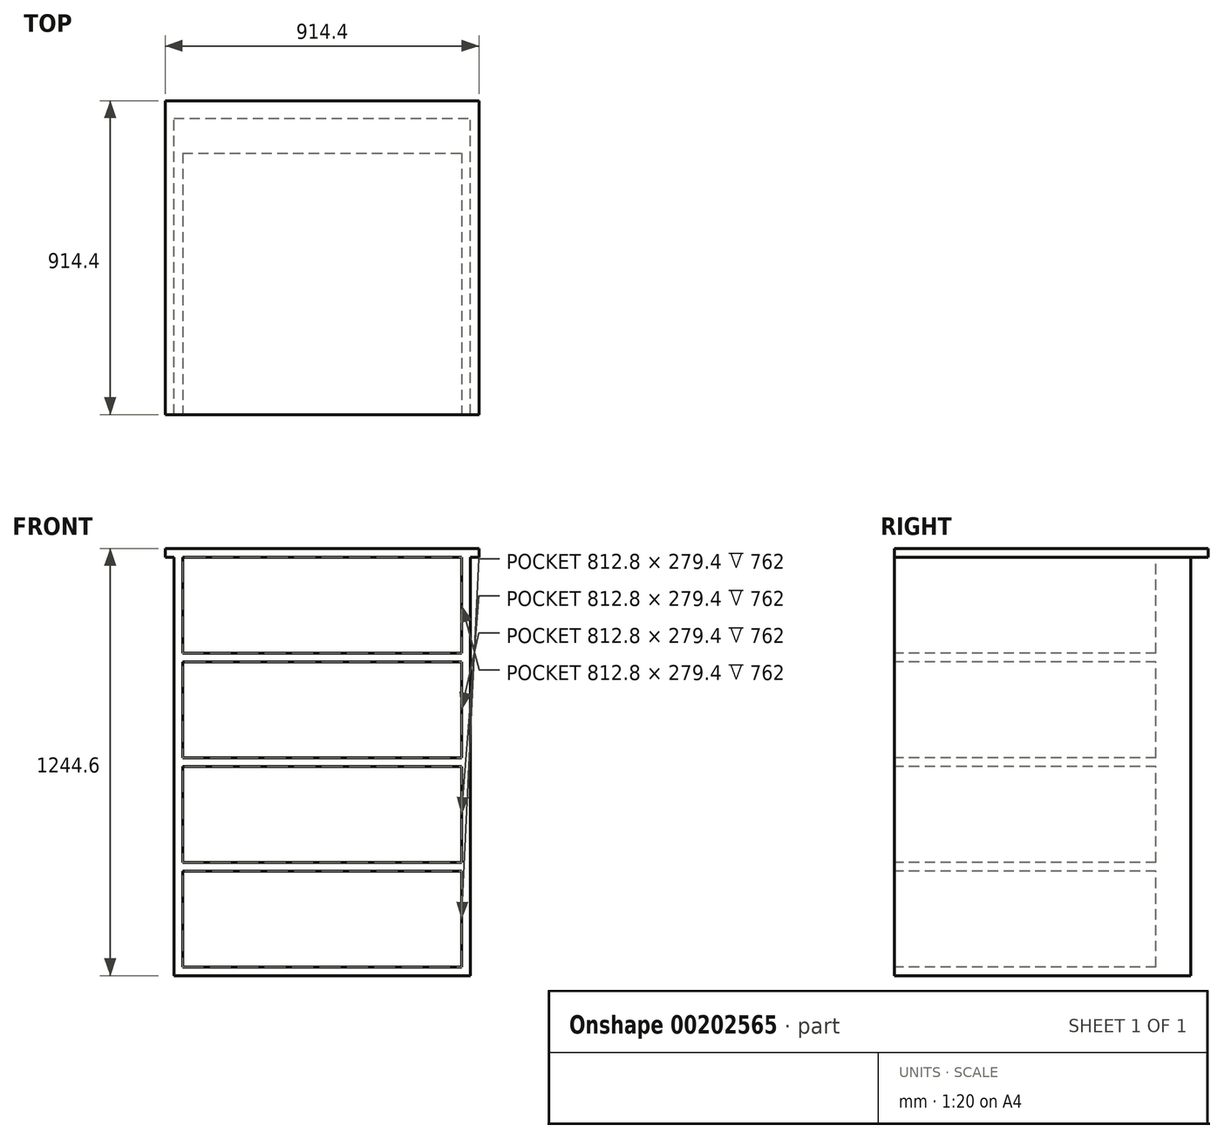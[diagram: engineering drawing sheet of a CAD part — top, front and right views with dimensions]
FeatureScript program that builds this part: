
annotation { "Feature Type Name" : "Feature", "Feature Type Description" : "" }
export const myFeature = defineFeature(function(context is Context, id is Id, definition is map)
    precondition{}
    {
        {
            var Q0;
            Q0=qCreatedBy(makeId("Top.planeOp"),FACE);
            var sketch = newSketch(context, id + "F0", { "sketchPlane" : qUnion([Q0])});
            skLineSegment(sketch, "E0.bottom", {"start": v(3.96, 0) * mm, "end": v(867.56, 0) * mm});
            skLineSegment(sketch, "E0.top", {"start": v(3.96, 863.6) * mm, "end": v(867.56, 863.6) * mm});
            skLineSegment(sketch, "E0.left", {"start": v(3.96, 0) * mm, "end": v(3.96, 863.6) * mm});
            skLineSegment(sketch, "E0.right", {"start": v(867.56, 0) * mm, "end": v(867.56, 863.6) * mm});
            skSolve(sketch);
        }
        {
            var Q0;
            Q0 = qSketchRegion(id + "F0", true);
            extrude(context, id + "F1", {"entities" : qUnion([Q0]), "depth" : 1219.2 * mm});
        }
        {
            var Q0;
            Q0=makeQuery(id+"F1.opExtrude","CAP_FACE",FACE,{"disambiguationData":[OSD([sQuery(id+"F0.wireOp",EDGE,"E0.bottom"),sQuery(id+"F0.wireOp",EDGE,"E0.top"),sQuery(id+"F0.wireOp",EDGE,"E0.left"),sQuery(id+"F0.wireOp",EDGE,"E0.right")])],"isStart":false});
            var sketch = newSketch(context, id + "F2", { "sketchPlane" : qUnion([Q0])});
            skLineSegment(sketch, "E1", {"start": v(867.56, 0) * mm, "end": v(892.96, 0) * mm});
            skLineSegment(sketch, "E2", {"start": v(892.96, 0) * mm, "end": v(892.96, 914.4) * mm});
            skLineSegment(sketch, "E3", {"start": v(892.96, 914.4) * mm, "end": v(-21.44, 914.4) * mm});
            skLineSegment(sketch, "E4", {"start": v(-21.44, 914.4) * mm, "end": v(-21.44, 0) * mm});
            skLineSegment(sketch, "E5", {"start": v(-21.44, 0) * mm, "end": v(3.96, 0) * mm});
            skLineSegment(sketch, "E6.bottom", {"start": v(867.56, 0) * mm, "end": v(3.96, 0) * mm});
            skLineSegment(sketch, "E6.top", {"start": v(867.56, 863.6) * mm, "end": v(3.96, 863.6) * mm});
            skLineSegment(sketch, "E6.left", {"start": v(867.56, 0) * mm, "end": v(867.56, 863.6) * mm});
            skLineSegment(sketch, "E6.right", {"start": v(3.96, 0) * mm, "end": v(3.96, 863.6) * mm});
            skSolve(sketch);
        }
        {
            var Q0;
            Q0 = qSketchRegion(id + "F2", true);
            extrude(context, id + "F3", {"entities" : qUnion([Q0]), "operationType" : NewBodyOperationType.ADD, "depth" : 25.4 * mm});
        }
        {
            var Q0;
            Q0=makeQuery(id+"F3.boolean.opBoolean","MERGE",FACE,{"derivedFrom":[makeQuery(id+"F1.opExtrude","SWEPT_FACE",FACE,{"disambiguationData":[OSD([sQuery(id+"F0.wireOp",EDGE,"E0.bottom")])]}),makeQuery(id+"F3.opExtrude","SWEPT_FACE",FACE,{"disambiguationData":[OSD([sQuery(id+"F2.wireOp",EDGE,"E1"),sQuery(id+"F2.wireOp",EDGE,"E5"),sQuery(id+"F2.wireOp",EDGE,"E6.bottom")])]})]});
            var sketch = newSketch(context, id + "F4", { "sketchPlane" : qUnion([Q0])});
            skLineSegment(sketch, "E7", {"start": v(3.96, 0) * mm, "end": v(3.96, 25.4) * mm});
            skLineSegment(sketch, "E8", {"start": v(3.96, 25.4) * mm, "end": v(29.36, 25.4) * mm});
            skLineSegment(sketch, "E9.bottom", {"start": v(29.36, 25.4) * mm, "end": v(842.16, 25.4) * mm});
            skLineSegment(sketch, "E9.top", {"start": v(29.36, 304.8) * mm, "end": v(842.16, 304.8) * mm});
            skLineSegment(sketch, "E9.left", {"start": v(29.36, 25.4) * mm, "end": v(29.36, 304.8) * mm});
            skLineSegment(sketch, "E9.right", {"start": v(842.16, 25.4) * mm, "end": v(842.16, 304.8) * mm});
            skLineSegment(sketch, "E10", {"start": v(29.36, 304.8) * mm, "end": v(29.36, 330.2) * mm});
            skLineSegment(sketch, "E11.bottom", {"start": v(29.36, 330.2) * mm, "end": v(842.16, 330.2) * mm});
            skLineSegment(sketch, "E11.top", {"start": v(29.36, 609.6) * mm, "end": v(842.16, 609.6) * mm});
            skLineSegment(sketch, "E11.left", {"start": v(29.36, 330.2) * mm, "end": v(29.36, 609.6) * mm});
            skLineSegment(sketch, "E11.right", {"start": v(842.16, 330.2) * mm, "end": v(842.16, 609.6) * mm});
            skLineSegment(sketch, "E12", {"start": v(29.36, 609.6) * mm, "end": v(29.36, 635) * mm});
            skLineSegment(sketch, "E13.bottom", {"start": v(29.36, 635) * mm, "end": v(842.16, 635) * mm});
            skLineSegment(sketch, "E13.top", {"start": v(29.36, 914.4) * mm, "end": v(842.16, 914.4) * mm});
            skLineSegment(sketch, "E13.left", {"start": v(29.36, 635) * mm, "end": v(29.36, 914.4) * mm});
            skLineSegment(sketch, "E13.right", {"start": v(842.16, 635) * mm, "end": v(842.16, 914.4) * mm});
            skLineSegment(sketch, "E14", {"start": v(29.36, 914.4) * mm, "end": v(29.36, 939.8) * mm});
            skLineSegment(sketch, "E15.bottom", {"start": v(29.36, 939.8) * mm, "end": v(842.16, 939.8) * mm});
            skLineSegment(sketch, "E15.top", {"start": v(29.36, 1219.2) * mm, "end": v(842.16, 1219.2) * mm});
            skLineSegment(sketch, "E15.left", {"start": v(29.36, 939.8) * mm, "end": v(29.36, 1219.2) * mm});
            skLineSegment(sketch, "E15.right", {"start": v(842.16, 939.8) * mm, "end": v(842.16, 1219.2) * mm});
            skSolve(sketch);
        }
        {
            var Q0;
            Q0=makeQuery(id+"F4.imprint","IMPRINT",FACE,{"disambiguationData":[TD([[makeQuery(id+"F4.imprint","IMPRINT",EDGE,{"derivedFrom":sQuery(id+"F4.wireOp",EDGE,"E15.bottom")}),1.0]])]});
            var Q1;
            Q1=makeQuery(id+"F4.imprint","IMPRINT",FACE,{"disambiguationData":[TD([[makeQuery(id+"F4.imprint","IMPRINT",EDGE,{"derivedFrom":sQuery(id+"F4.wireOp",EDGE,"E13.bottom")}),1.0]])]});
            var Q2;
            Q2=makeQuery(id+"F4.imprint","IMPRINT",FACE,{"disambiguationData":[TD([[makeQuery(id+"F4.imprint","IMPRINT",EDGE,{"derivedFrom":sQuery(id+"F4.wireOp",EDGE,"E11.bottom")}),1.0]])]});
            var Q3;
            Q3=makeQuery(id+"F4.imprint","IMPRINT",FACE,{"disambiguationData":[TD([[makeQuery(id+"F4.imprint","IMPRINT",EDGE,{"derivedFrom":sQuery(id+"F4.wireOp",EDGE,"E9.bottom")}),1.0]])]});
            extrude(context, id + "F5", {"entities" : qUnion([Q0, Q1, Q2, Q3]), "operationType" : NewBodyOperationType.REMOVE, "oppositeDirection" : true, "depth" : 762 * mm});
        }
    });
